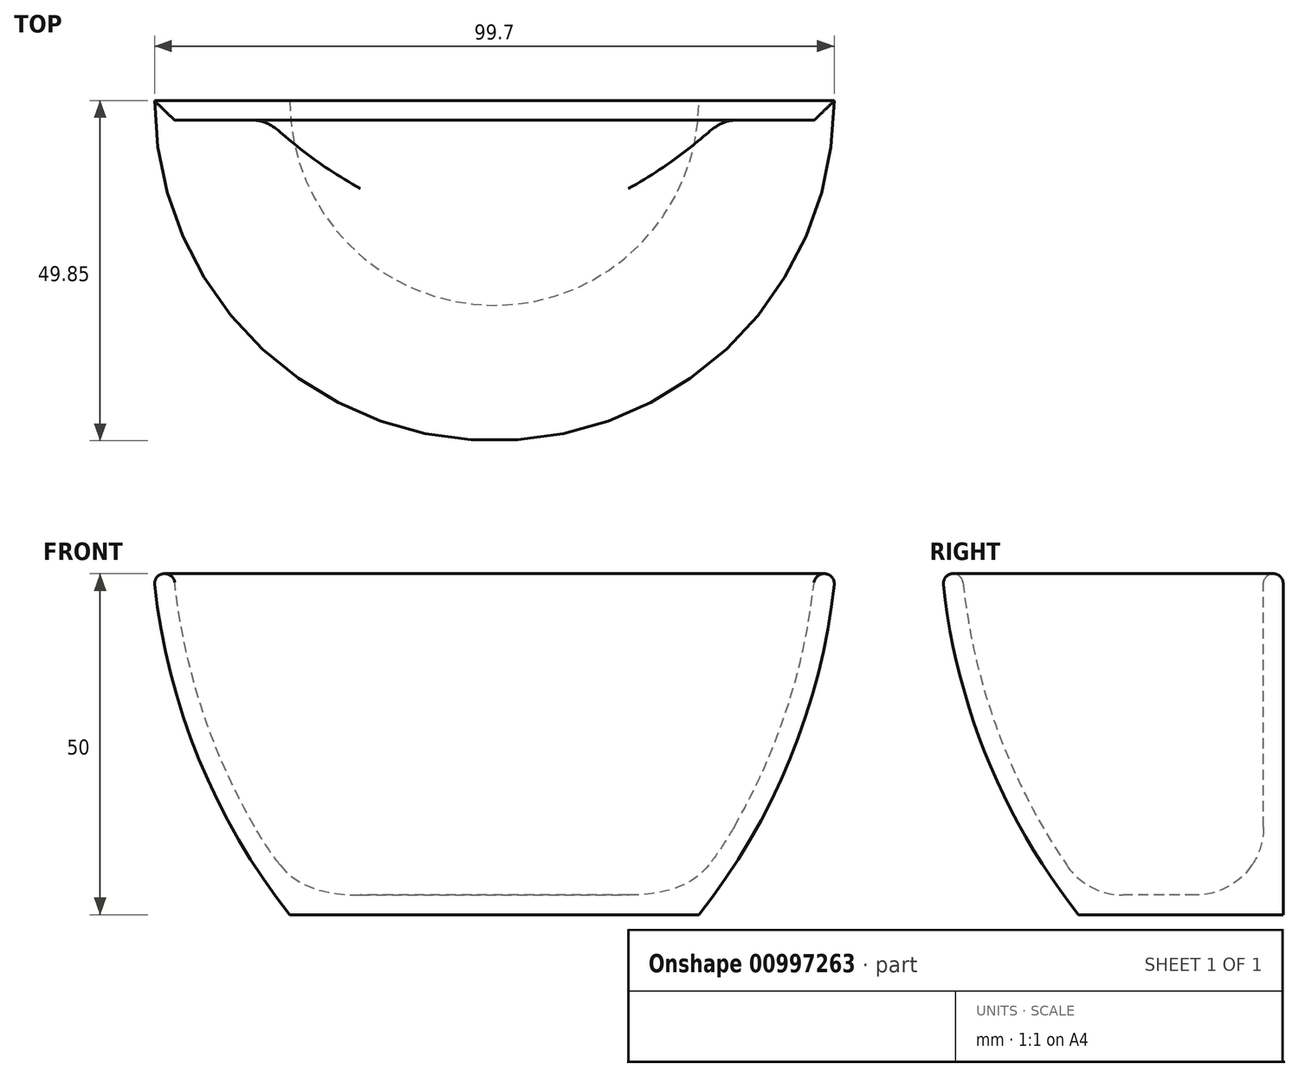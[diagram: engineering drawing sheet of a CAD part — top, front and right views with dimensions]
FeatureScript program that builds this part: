
annotation { "Feature Type Name" : "Feature", "Feature Type Description" : "" }
export const myFeature = defineFeature(function(context is Context, id is Id, definition is map)
    precondition{}
    {
        {
            assignVariable(context, id + "F0", {"name" : "wallthickness", "anyValue" : 0.72 * 4});
        }
        {
            var Q0;
            Q0=qCreatedBy(makeId("Front.planeOp"),FACE);
            var sketch = newSketch(context, id + "F1", { "sketchPlane" : qUnion([Q0])});
            skLineSegment(sketch, "E0", {"start": v(0, 0) * mm, "end": v(30, 0) * mm});
            skLineSegment(sketch, "E1", {"start": v(0, 0) * mm, "end": v(0, 50) * mm});
            skLineSegment(sketch, "E2", {"start": v(0, 50) * mm, "end": v(50, 50) * mm});
            skArc(sketch, "E3", {"start": v(30, 0) * mm, "mid": v(43.65, 23.54) * mm, "end": v(50, 50) * mm});
            skSolve(sketch);
        }
        {
            var Q0;
            Q0=makeQuery(id+"F1.imprint","IMPRINT",FACE,{"disambiguationData":[TD([[makeQuery(id+"F1.imprint","IMPRINT",EDGE,{"derivedFrom":sQuery(id+"F1.wireOp",EDGE,"E0")}),1.0]])]});
            var Q1;
            Q1=sQuery(id+"F1.wireOp",EDGE,"E1");
            revolve(context, id + "F2", {"surfaceOperationType" : NewSurfaceOperationType.NEW, "entities" : qUnion([Q0]), "axis" : qUnion([Q1]), "revolveType" : RevolveType.ONE_DIRECTION, "oppositeDirection" : true, "angle" : 180 * degree});
        }
        {
            var Q0;
            Q0=makeQuery(id+"F2.opRevolve","SWEPT_FACE",FACE,{"disambiguationData":[OSD([sQuery(id+"F1.wireOp",EDGE,"E2")])]});
            shell(context, id + "F3", {"entities" : qUnion([Q0]), "thickness" : (getVariable(context, 'wallthickness')) * mm});
        }
        {
            var Q0;
            Q0=makeQuery(id+"F3.opShell","OFFSET_FACE",FACE,{"disambiguationData":[OSD([sQuery(id+"F1.wireOp",EDGE,"E0")])]});
            fillet(context, id + "F4", {"entities" : qUnion([Q0]), "radius" : 10 * mm, "tangentPropagation" : true, "allowEdgeOverflow" : false});
        }
        {
            var Q0;
            Q0=makeQuery(id+"F2.opRevolve","SWEPT_FACE",FACE,{"disambiguationData":[OSD([sQuery(id+"F1.wireOp",EDGE,"E2")])]});
            fillet(context, id + "F5", {"entities" : qUnion([Q0]), "radius" : (getVariable(context, 'wallthickness') / 2) * mm, "tangentPropagation" : true, "allowEdgeOverflow" : false});
        }
    });
